# Revit family: PRD_FrankeWS_ShwrFttngsPckg_InstallationSet_ZSHOW0013
name_source: partatom
category: Pipe Fittings
revit_build: Autodesk Revit 2018 (Build: 20190510_1515(x64)
units: mm (PartAtom-declared; Revit-internal decimal feet)

## family parameters
Always vertical = Yes
Cut with Voids When Loaded = Yes
OmniClass Number = 23.45.55.11
OmniClass Title = Sanitary Components
Part Type = Elbow
Round Connector Dimension = Use Diameter
Shared = No
Work Plane-Based = No

## types (1)
- ZSHOW0013
    AssetType = Fixed
    BIMObjectName = PRD_AR_ShowerFittingsPackage_InstallationSet_ZSHOW0013
    BodyMaterial = <By Category>
    Category = Pr_40_20_87_75, Shower fittings package
    Description = Installation set for water from the wall above the SMARTWAVE shower panel. Consisting of lockable wall angles and rosette.
    DiameterNominal1 = 15  [stored 0.0492126 ft]
    DiameterNominal2 = 20  [stored 0.0656168 ft]
    DurationUnit = year
    Features = Consisting of lockable wall angles and rosette
    GrossWeight = 0.25 kg
    IfcExportAs = IfcSanitaryTerminalType
    IfcExportType = USERDEFINED
    Manufacturer = KWC Group AG
    ManufacturerName = KWC Group AG
    ManufacturerURL = www.kwc.com
    Model = ZSHOW0013
    ModelNumber = 2030008547
    ModelReference = ZSHOW0013
    NBSDescription = Shower fittings package
    NBSReference = 45-35-70/330
    Name = Installation set ZSHOW0013
    NetWeight = 0.24 kg
    NominalDepth = 0 mm  [stored 0 ft]
    NominalHeight = 0 mm  [stored 0 ft]
    NominalLength = 0 mm  [stored 0 ft]
    NominalWidth = 0 mm  [stored 0 ft]
    ProductInformation = https://pim.kwc.com
    Quantity = 2
    QuantityUom = Pieces
    Status = New
    TailorMade = No
    URL = www.kwc.com
    Uniclass2015Code = Pr_40_20_87_75
    Uniclass2015Title = Shower fittings package
    Uniclass2015Version = Products v1.23
    Version = 1
    WarrantyDurationUnit = year

note: [stored X ft] marks values corroborated as IEEE doubles in the binary element streams (Revit-internal decimal feet)

## geometry (parser evidence)
native form markers: Sweep x3
no freeform markers — native parametric forms only
